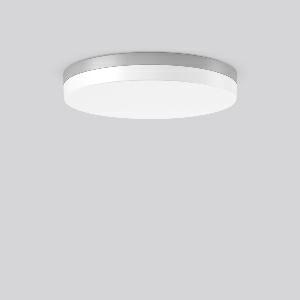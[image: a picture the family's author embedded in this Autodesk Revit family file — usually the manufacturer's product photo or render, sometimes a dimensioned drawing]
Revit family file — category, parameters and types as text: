
# Revit family: flat_slim_round_312634_004_32b0
name_source: partatom
category: Lighting Fixtures
units: mm (PartAtom-declared; Revit-internal decimal feet)

## family parameters
Cut with Voids When Loaded = No
Host = Face
Light Source = No
Part Type = Normal
Room Calculation Point = No
Round Connector Dimension = Use Diameter
Shared = No

## types (1)
- MultiLumen 1 830 (1 x LED Modul 830, 3450 lm, 3000)
    Apparent Load = 26 VA
    CIE Flux Codes = 40 71 90 84 100
    Color Rendering = 80
    Color Temperature = 3000
    Default Elevation = 1800 mm
    Height = 70 mm
    Lamp = 1 x LED Modul 830
    Lamp Light Flux = 3450 lm
    Lamp count = 1
    Length = 480 mm
    Lifetime = 50000 h
    Luminous efficacy = 133 lm/W
    Manufacturer = RZB
    ModVariant = No
    Model = 312634.004
    Mounting Place = Ceiling
    Mounting Type = Surface mounted
    Number of Poles = 1
    OnlyDefault = Yes
    Power Factor = 1
    Product Name = FLAT SLIM round
    Product group = Surface mounted ceiling and wall luminaires
    ProductGroupID = 305
    Protection Class = Protection class I
    Protection Degree = Degree of protection
    RLX_Detail_Level = 1
    RLX_Emergency_Light_Flux = 0 lm
    RLX_Emergency_Type = 0
    RLX_Emergency_Type_DB = No
    RlxData = <blob elided: 21665 chars, md5=31b87ddb>
    Socket = socket
    Standby Power = 0 W
    System Light Flux = 3450 lm
    System Power = 26 W
    Type Comments = MultiLumen 1 830
    Type Image = 312633.004.jpg
    URL = http://relux.com
    VarID = multilumen_1_830
    Voltage = 0 V
    Weight = 0.00 kg
    Width = 0 mm  [stored 0 ft]

note: [stored X ft] marks values corroborated as IEEE doubles in the binary element streams (Revit-internal decimal feet)

## geometry (parser evidence)
native form markers: Blend x4, Sweep x15
no freeform markers — native parametric forms only
